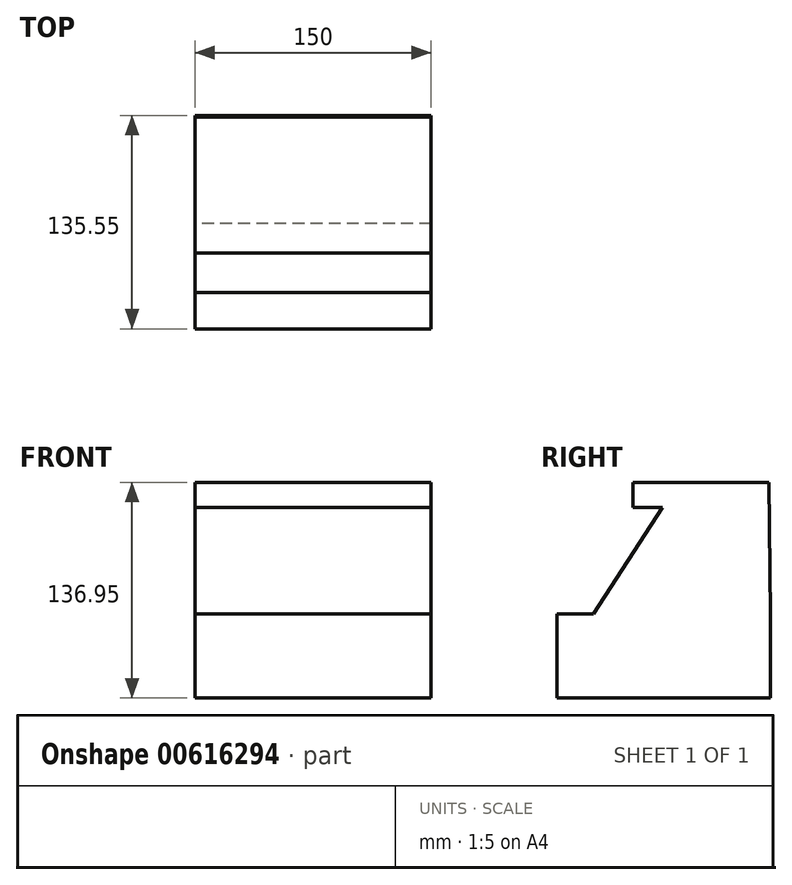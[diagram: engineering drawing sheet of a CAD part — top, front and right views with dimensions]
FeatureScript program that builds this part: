
annotation { "Feature Type Name" : "Feature", "Feature Type Description" : "" }
export const myFeature = defineFeature(function(context is Context, id is Id, definition is map)
    precondition{}
    {
        {
            var Q0;
            Q0=qCreatedBy(makeId("Right.planeOp"),FACE);
            var sketch = newSketch(context, id + "F0", { "sketchPlane" : qUnion([Q0])});
            skPoint(sketch, "E0.middle", {"position": v(0, 0) * mm});
            skLineSegment(sketch, "E1.bottom", {"start": v(-67.05, -63.04) * mm, "end": v(68.5, -63.04) * mm});
            skLineSegment(sketch, "E1.left", {"start": v(-67.05, -63.04) * mm, "end": v(-67.05, -9.53) * mm});
            skLineSegment(sketch, "E1.right", {"start": v(68.5, -63.04) * mm, "end": v(68.5, -9.53) * mm});
            skLineSegment(sketch, "E2", {"start": v(-43.81, -9.53) * mm, "end": v(0, 58.07) * mm});
            skLineSegment(sketch, "E3", {"start": v(0, 58.07) * mm, "end": v(-18.81, 58.07) * mm});
            skLineSegment(sketch, "E4", {"start": v(-18.81, 73.91) * mm, "end": v(-18.81, 58.07) * mm});
            skLineSegment(sketch, "E5", {"start": v(-18.81, 73.91) * mm, "end": v(67.44, 73.91) * mm});
            skLineSegment(sketch, "E6", {"start": v(68.5, -9.53) * mm, "end": v(67.44, 73.91) * mm});
            skLineSegment(sketch, "E7", {"start": v(-67.05, -9.53) * mm, "end": v(-43.81, -9.53) * mm});
            skSolve(sketch);
        }
        {
            var Q0;
            Q0 = qSketchRegion(id + "F0", true);
            extrude(context, id + "F1", {"entities" : qUnion([Q0]), "endBound" : BoundingType.SYMMETRIC, "depth" : 150 * mm, "offsetDistance" : 25 * mm});
        }
    });
